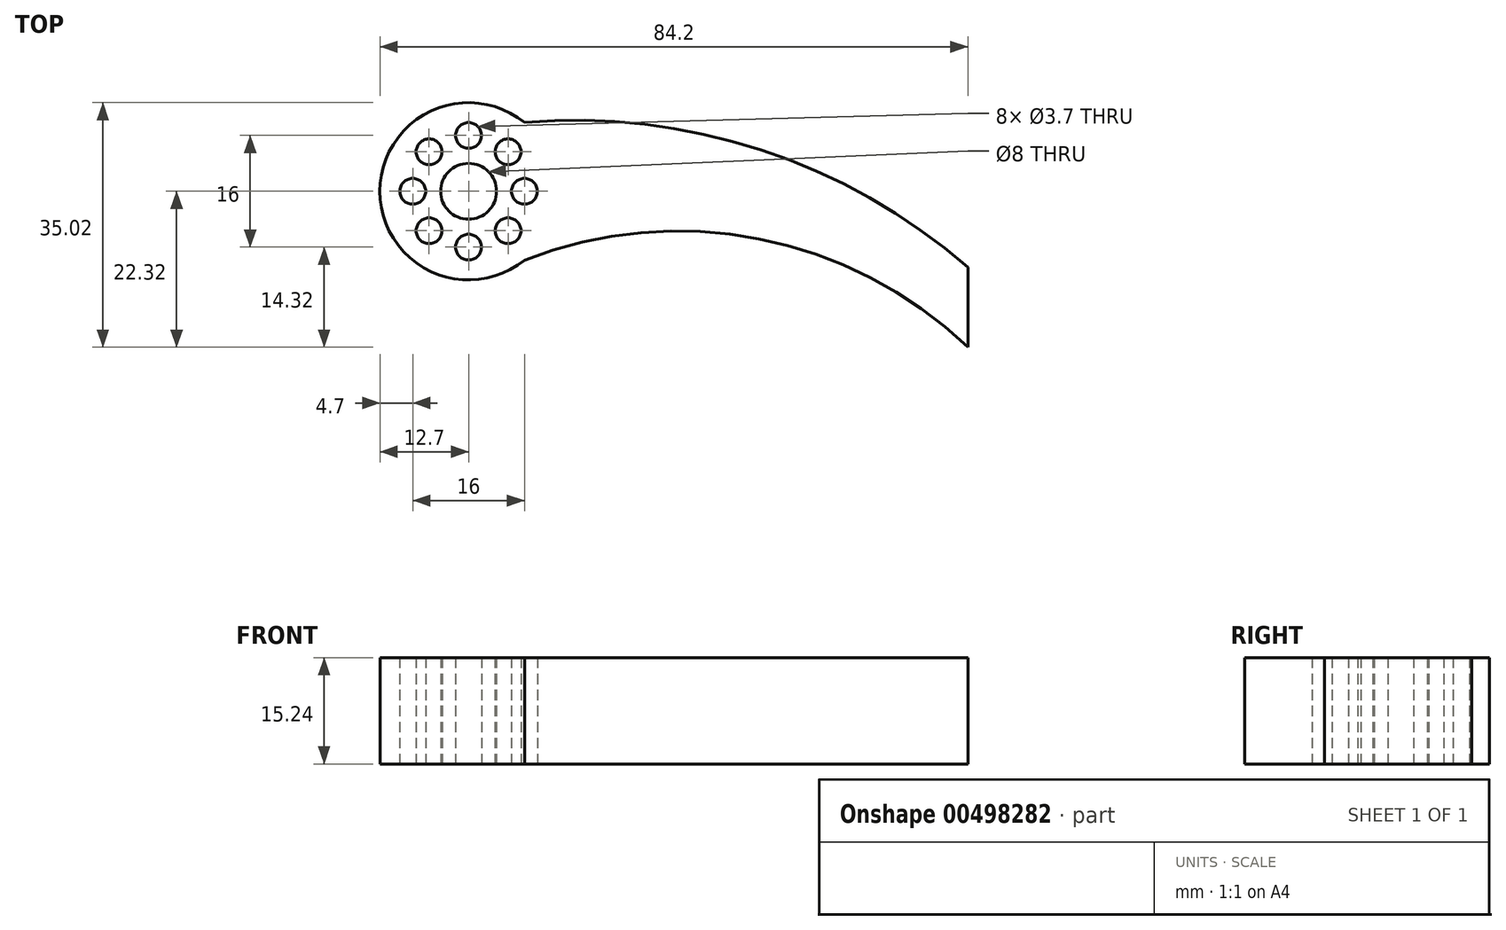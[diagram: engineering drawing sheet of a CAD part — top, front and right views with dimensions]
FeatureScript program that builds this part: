
annotation { "Feature Type Name" : "Feature", "Feature Type Description" : "" }
export const myFeature = defineFeature(function(context is Context, id is Id, definition is map)
    precondition{}
    {
        {
            var Q0;
            Q0=qCreatedBy(makeId("Top.planeOp"),FACE);
            var sketch = newSketch(context, id + "F0", { "sketchPlane" : qUnion([Q0])});
            skCircle(sketch, "E0", {"center": v(0, 0) * mm, "radius": 12.7 * mm});
            skPoint(sketch, "E1", {"position": v(8, 0) * mm});
            skPoint(sketch, "E2", {"position": v(8, -15.24) * mm});
            skPoint(sketch, "E3.start.orphan", {"position": v(71.5, 0) * mm});
            skPoint(sketch, "E4.orphan", {"position": v(8, -9.86) * mm});
            skPoint(sketch, "E5", {"position": v(8, -7.08) * mm});
            skPoint(sketch, "E6", {"position": v(8, -22.32) * mm});
            skPoint(sketch, "E7.start.orphan", {"position": v(8, 9.86) * mm});
            skPoint(sketch, "E8.end.orphan", {"position": v(71.5, -22.32) * mm});
            skPoint(sketch, "E8.start.orphan", {"position": v(71.5, -7.08) * mm});
            skArc(sketch, "E9", {"start": v(71.5, -22.32) * mm, "mid": v(41.57, -6.82) * mm, "end": v(8, -9.86) * mm});
            skLineSegment(sketch, "E10", {"start": v(71.5, -22.32) * mm, "end": v(71.5, -10.89) * mm});
            skPoint(sketch, "E11", {"position": v(71.5, -10.89) * mm});
            skArc(sketch, "E12", {"start": v(71.5, -10.89) * mm, "mid": v(41.86, 5.94) * mm, "end": v(8, 9.86) * mm});
            skCircle(sketch, "E13", {"center": v(0, 0) * mm, "radius": 4 * mm});
            skCircle(sketch, "E14", {"center": v(0, 8) * mm, "radius": 1.85 * mm});
            skCircle(sketch, "E15.1.0", {"center": v(-5.66, 5.66) * mm, "radius": 1.85 * mm});
            skCircle(sketch, "E15.2.0", {"center": v(-8, 0) * mm, "radius": 1.85 * mm});
            skCircle(sketch, "E15.3.0", {"center": v(-5.66, -5.66) * mm, "radius": 1.85 * mm});
            skCircle(sketch, "E15.4.0", {"center": v(0, -8) * mm, "radius": 1.85 * mm});
            skCircle(sketch, "E15.5.0", {"center": v(5.66, -5.66) * mm, "radius": 1.85 * mm});
            skCircle(sketch, "E15.6.0", {"center": v(8, 0) * mm, "radius": 1.85 * mm});
            skCircle(sketch, "E15.7.0", {"center": v(5.66, 5.66) * mm, "radius": 1.85 * mm});
            skSolve(sketch);
        }
        {
            var Q0;
            Q0 = qSketchRegion(id + "F0", true);
            extrude(context, id + "F1", {"entities" : qUnion([Q0]), "depth" : 15.24 * mm});
        }
    });
